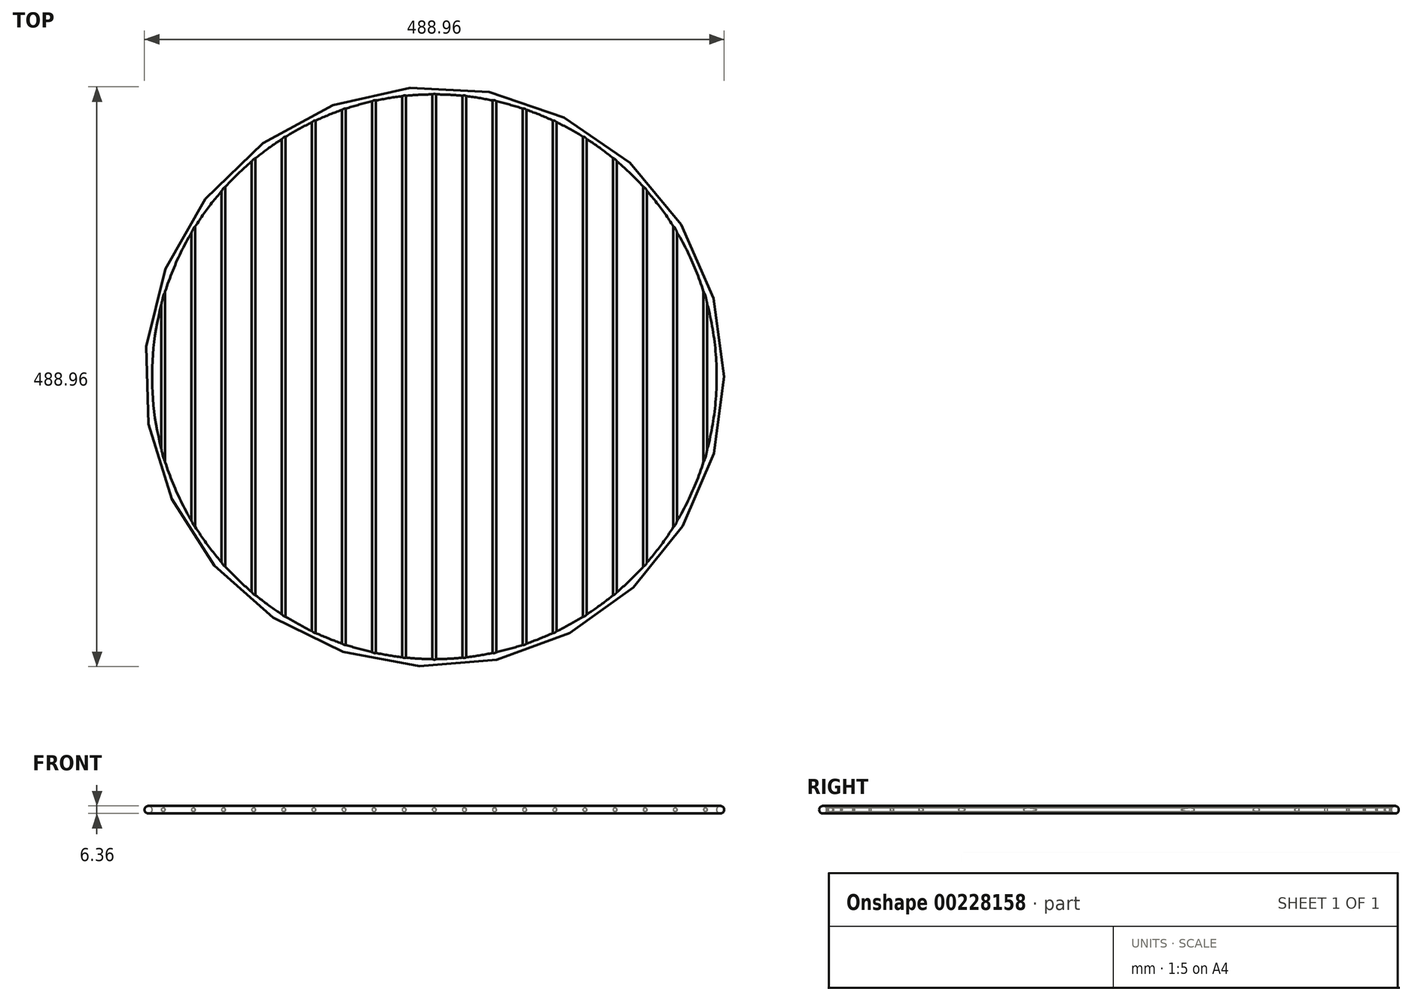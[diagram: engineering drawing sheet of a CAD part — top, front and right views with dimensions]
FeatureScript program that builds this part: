
annotation { "Feature Type Name" : "Feature", "Feature Type Description" : "" }
export const myFeature = defineFeature(function(context is Context, id is Id, definition is map)
    precondition{}
    {
        {
            var Q0;
            Q0=qCreatedBy(makeId("Front.planeOp"),FACE);
            var sketch = newSketch(context, id + "F0", { "sketchPlane" : qUnion([Q0])});
            skCircle(sketch, "E0", {"center": v(241.3, 0) * mm, "radius": 3.18 * mm});
            skLineSegment(sketch, "E1", {"start": v(0, 0) * mm, "end": v(0, 32.12) * mm, "construction": true});
            skSolve(sketch);
        }
        {
            var Q0;
            Q0=qCreatedBy(makeId("Front.planeOp"),FACE);
            var sketch = newSketch(context, id + "F1", { "sketchPlane" : qUnion([Q0])});
            skCircle(sketch, "E2", {"center": v(0, 0) * mm, "radius": 1.59 * mm});
            skCircle(sketch, "E3.1.0.0", {"center": v(25.4, 0) * mm, "radius": 1.59 * mm});
            skCircle(sketch, "E3.2.0.0", {"center": v(50.8, 0) * mm, "radius": 1.59 * mm});
            skCircle(sketch, "E3.3.0.0", {"center": v(76.2, 0) * mm, "radius": 1.59 * mm});
            skCircle(sketch, "E3.4.0.0", {"center": v(101.6, 0) * mm, "radius": 1.59 * mm});
            skCircle(sketch, "E3.5.0.0", {"center": v(127, 0) * mm, "radius": 1.59 * mm});
            skCircle(sketch, "E3.6.0.0", {"center": v(152.4, 0) * mm, "radius": 1.59 * mm});
            skCircle(sketch, "E3.7.0.0", {"center": v(177.8, 0) * mm, "radius": 1.59 * mm});
            skCircle(sketch, "E3.8.0.0", {"center": v(203.2, 0) * mm, "radius": 1.59 * mm});
            skCircle(sketch, "E3.9.0.0", {"center": v(228.6, 0) * mm, "radius": 1.59 * mm});
            skLineSegment(sketch, "E3.direction1", {"start": v(0, 0) * mm, "end": v(25.4, 0) * mm, "construction": true});
            skCircle(sketch, "E4.1.0.0", {"center": v(-25.4, 0) * mm, "radius": 1.59 * mm});
            skCircle(sketch, "E4.2.0.0", {"center": v(-50.8, 0) * mm, "radius": 1.59 * mm});
            skCircle(sketch, "E4.3.0.0", {"center": v(-76.2, 0) * mm, "radius": 1.59 * mm});
            skCircle(sketch, "E4.4.0.0", {"center": v(-101.6, 0) * mm, "radius": 1.59 * mm});
            skCircle(sketch, "E4.5.0.0", {"center": v(-127, 0) * mm, "radius": 1.59 * mm});
            skCircle(sketch, "E4.6.0.0", {"center": v(-152.4, 0) * mm, "radius": 1.59 * mm});
            skCircle(sketch, "E4.7.0.0", {"center": v(-177.8, 0) * mm, "radius": 1.59 * mm});
            skCircle(sketch, "E4.8.0.0", {"center": v(-203.2, 0) * mm, "radius": 1.59 * mm});
            skCircle(sketch, "E4.9.0.0", {"center": v(-228.6, 0) * mm, "radius": 1.59 * mm});
            skLineSegment(sketch, "E4.direction1", {"start": v(0, 0) * mm, "end": v(-25.4, 0) * mm, "construction": true});
            skSolve(sketch);
        }
        {
            var Q0;
            Q0=makeQuery(id+"F0.imprint","IMPRINT",FACE,{"disambiguationData":[TD([[makeQuery(id+"F0.imprint","IMPRINT",EDGE,{"derivedFrom":sQuery(id+"F0.wireOp",EDGE,"E0")}),1.0]])]});
            var Q1;
            Q1=sQuery(id+"F0.wireOp",EDGE,"E1");
            revolve(context, id + "F2", {"entities" : qUnion([Q0]), "axis" : qUnion([Q1]), "revolveType" : RevolveType.FULL});
        }
        {
            var Q0;
            Q0=makeQuery(id+"F1.imprint","IMPRINT",FACE,{"disambiguationData":[TD([[makeQuery(id+"F1.imprint","IMPRINT",EDGE,{"derivedFrom":sQuery(id+"F1.wireOp",EDGE,"E3.1.0.0")}),1.0]])]});
            var Q1;
            Q1=makeQuery(id+"F1.imprint","IMPRINT",FACE,{"disambiguationData":[TD([[makeQuery(id+"F1.imprint","IMPRINT",EDGE,{"derivedFrom":sQuery(id+"F1.wireOp",EDGE,"E3.7.0.0")}),1.0]])]});
            var Q2;
            Q2=makeQuery(id+"F1.imprint","IMPRINT",FACE,{"disambiguationData":[TD([[makeQuery(id+"F1.imprint","IMPRINT",EDGE,{"derivedFrom":sQuery(id+"F1.wireOp",EDGE,"E3.6.0.0")}),1.0]])]});
            var Q3;
            Q3=makeQuery(id+"F1.imprint","IMPRINT",FACE,{"disambiguationData":[TD([[makeQuery(id+"F1.imprint","IMPRINT",EDGE,{"derivedFrom":sQuery(id+"F1.wireOp",EDGE,"E3.2.0.0")}),1.0]])]});
            var Q4;
            Q4=makeQuery(id+"F1.imprint","IMPRINT",FACE,{"disambiguationData":[TD([[makeQuery(id+"F1.imprint","IMPRINT",EDGE,{"derivedFrom":sQuery(id+"F1.wireOp",EDGE,"E3.3.0.0")}),1.0]])]});
            var Q5;
            Q5=makeQuery(id+"F1.imprint","IMPRINT",FACE,{"disambiguationData":[TD([[makeQuery(id+"F1.imprint","IMPRINT",EDGE,{"derivedFrom":sQuery(id+"F1.wireOp",EDGE,"E3.4.0.0")}),1.0]])]});
            var Q6;
            Q6=makeQuery(id+"F1.imprint","IMPRINT",FACE,{"disambiguationData":[TD([[makeQuery(id+"F1.imprint","IMPRINT",EDGE,{"derivedFrom":sQuery(id+"F1.wireOp",EDGE,"E3.5.0.0")}),1.0]])]});
            var Q7;
            Q7=makeQuery(id+"F1.imprint","IMPRINT",FACE,{"disambiguationData":[TD([[makeQuery(id+"F1.imprint","IMPRINT",EDGE,{"derivedFrom":sQuery(id+"F1.wireOp",EDGE,"E3.8.0.0")}),1.0]])]});
            var Q8;
            Q8=makeQuery(id+"F1.imprint","IMPRINT",FACE,{"disambiguationData":[TD([[makeQuery(id+"F1.imprint","IMPRINT",EDGE,{"derivedFrom":sQuery(id+"F1.wireOp",EDGE,"E3.9.0.0")}),1.0]])]});
            var Q9;
            Q9=makeQuery(id+"F1.imprint","IMPRINT",FACE,{"disambiguationData":[TD([[makeQuery(id+"F1.imprint","IMPRINT",EDGE,{"derivedFrom":sQuery(id+"F1.wireOp",EDGE,"E4.9.0.0")}),1.0]])]});
            var Q10;
            Q10=makeQuery(id+"F1.imprint","IMPRINT",FACE,{"disambiguationData":[TD([[makeQuery(id+"F1.imprint","IMPRINT",EDGE,{"derivedFrom":sQuery(id+"F1.wireOp",EDGE,"E4.2.0.0")}),1.0]])]});
            var Q11;
            Q11=makeQuery(id+"F1.imprint","IMPRINT",FACE,{"disambiguationData":[TD([[makeQuery(id+"F1.imprint","IMPRINT",EDGE,{"derivedFrom":sQuery(id+"F1.wireOp",EDGE,"E4.3.0.0")}),1.0]])]});
            var Q12;
            Q12=makeQuery(id+"F1.imprint","IMPRINT",FACE,{"disambiguationData":[TD([[makeQuery(id+"F1.imprint","IMPRINT",EDGE,{"derivedFrom":sQuery(id+"F1.wireOp",EDGE,"E4.7.0.0")}),1.0]])]});
            var Q13;
            Q13=makeQuery(id+"F1.imprint","IMPRINT",FACE,{"disambiguationData":[TD([[makeQuery(id+"F1.imprint","IMPRINT",EDGE,{"derivedFrom":sQuery(id+"F1.wireOp",EDGE,"E4.8.0.0")}),1.0]])]});
            var Q14;
            Q14=makeQuery(id+"F1.imprint","IMPRINT",FACE,{"disambiguationData":[TD([[makeQuery(id+"F1.imprint","IMPRINT",EDGE,{"derivedFrom":sQuery(id+"F1.wireOp",EDGE,"E4.6.0.0")}),1.0]])]});
            var Q15;
            Q15=makeQuery(id+"F1.imprint","IMPRINT",FACE,{"disambiguationData":[TD([[makeQuery(id+"F1.imprint","IMPRINT",EDGE,{"derivedFrom":sQuery(id+"F1.wireOp",EDGE,"E4.4.0.0")}),1.0]])]});
            var Q16;
            Q16=makeQuery(id+"F1.imprint","IMPRINT",FACE,{"disambiguationData":[TD([[makeQuery(id+"F1.imprint","IMPRINT",EDGE,{"derivedFrom":sQuery(id+"F1.wireOp",EDGE,"E4.5.0.0")}),1.0]])]});
            var Q17;
            Q17=makeQuery(id+"F1.imprint","IMPRINT",FACE,{"disambiguationData":[TD([[makeQuery(id+"F1.imprint","IMPRINT",EDGE,{"derivedFrom":sQuery(id+"F1.wireOp",EDGE,"E4.1.0.0")}),1.0]])]});
            var Q18;
            Q18=makeQuery(id+"F1.imprint","IMPRINT",FACE,{"disambiguationData":[TD([[makeQuery(id+"F1.imprint","IMPRINT",EDGE,{"derivedFrom":sQuery(id+"F1.wireOp",EDGE,"E2")}),1.0]])]});
            var Q19;
            Q19=sQuery(id+"F1.wireOp",EDGE,"E2");
            var Q20;
            Q20=sQuery(id+"F1.wireOp",EDGE,"E3.1.0.0");
            var Q21;
            Q21=sQuery(id+"F1.wireOp",EDGE,"E3.2.0.0");
            var Q22;
            Q22=sQuery(id+"F1.wireOp",EDGE,"E3.3.0.0");
            var Q23;
            Q23=sQuery(id+"F1.wireOp",EDGE,"E3.4.0.0");
            var Q24;
            Q24=sQuery(id+"F1.wireOp",EDGE,"E3.5.0.0");
            var Q25;
            Q25=sQuery(id+"F1.wireOp",EDGE,"E3.6.0.0");
            var Q26;
            Q26=sQuery(id+"F1.wireOp",EDGE,"E3.7.0.0");
            var Q27;
            Q27=sQuery(id+"F1.wireOp",EDGE,"E3.8.0.0");
            var Q28;
            Q28=sQuery(id+"F1.wireOp",EDGE,"E3.9.0.0");
            var Q29;
            Q29=sQuery(id+"F1.wireOp",EDGE,"E4.1.0.0");
            var Q30;
            Q30=sQuery(id+"F1.wireOp",EDGE,"E4.2.0.0");
            var Q31;
            Q31=sQuery(id+"F1.wireOp",EDGE,"E4.3.0.0");
            var Q32;
            Q32=sQuery(id+"F1.wireOp",EDGE,"E4.4.0.0");
            var Q33;
            Q33=sQuery(id+"F1.wireOp",EDGE,"E4.5.0.0");
            var Q34;
            Q34=sQuery(id+"F1.wireOp",EDGE,"E4.6.0.0");
            var Q35;
            Q35=sQuery(id+"F1.wireOp",EDGE,"E4.7.0.0");
            var Q36;
            Q36=sQuery(id+"F1.wireOp",EDGE,"E4.8.0.0");
            var Q37;
            Q37=sQuery(id+"F1.wireOp",EDGE,"E4.9.0.0");
            var Q38;
            Q38=makeQuery(id+"F2.opRevolve","SWEPT_BODY",BODY,{"disambiguationData":[OSD([sQuery(id+"F0.wireOp",EDGE,"E0")])]});
            extrude(context, id + "F3", {"entities" : qUnion([Q0, Q1, Q2, Q3, Q4, Q5, Q6, Q7, Q8, Q9, Q10, Q11, Q12, Q13, Q14, Q15, Q16, Q17, Q18]), "operationType" : NewBodyOperationType.ADD, "surfaceEntities" : qUnion([Q19, Q20, Q21, Q22, Q23, Q24, Q25, Q26, Q27, Q28, Q29, Q30, Q31, Q32, Q33, Q34, Q35, Q36, Q37]), "endBound" : BoundingType.UP_TO_NEXT, "depth" : 254 * mm, "hasSecondDirection" : true, "secondDirectionBound" : SecondDirectionBoundingType.UP_TO_NEXT, "secondDirectionOppositeDirection" : true, "secondDirectionBoundEntityBody" : qUnion([Q38]), "secondDirectionDepth" : 25.4 * mm});
        }
    });
